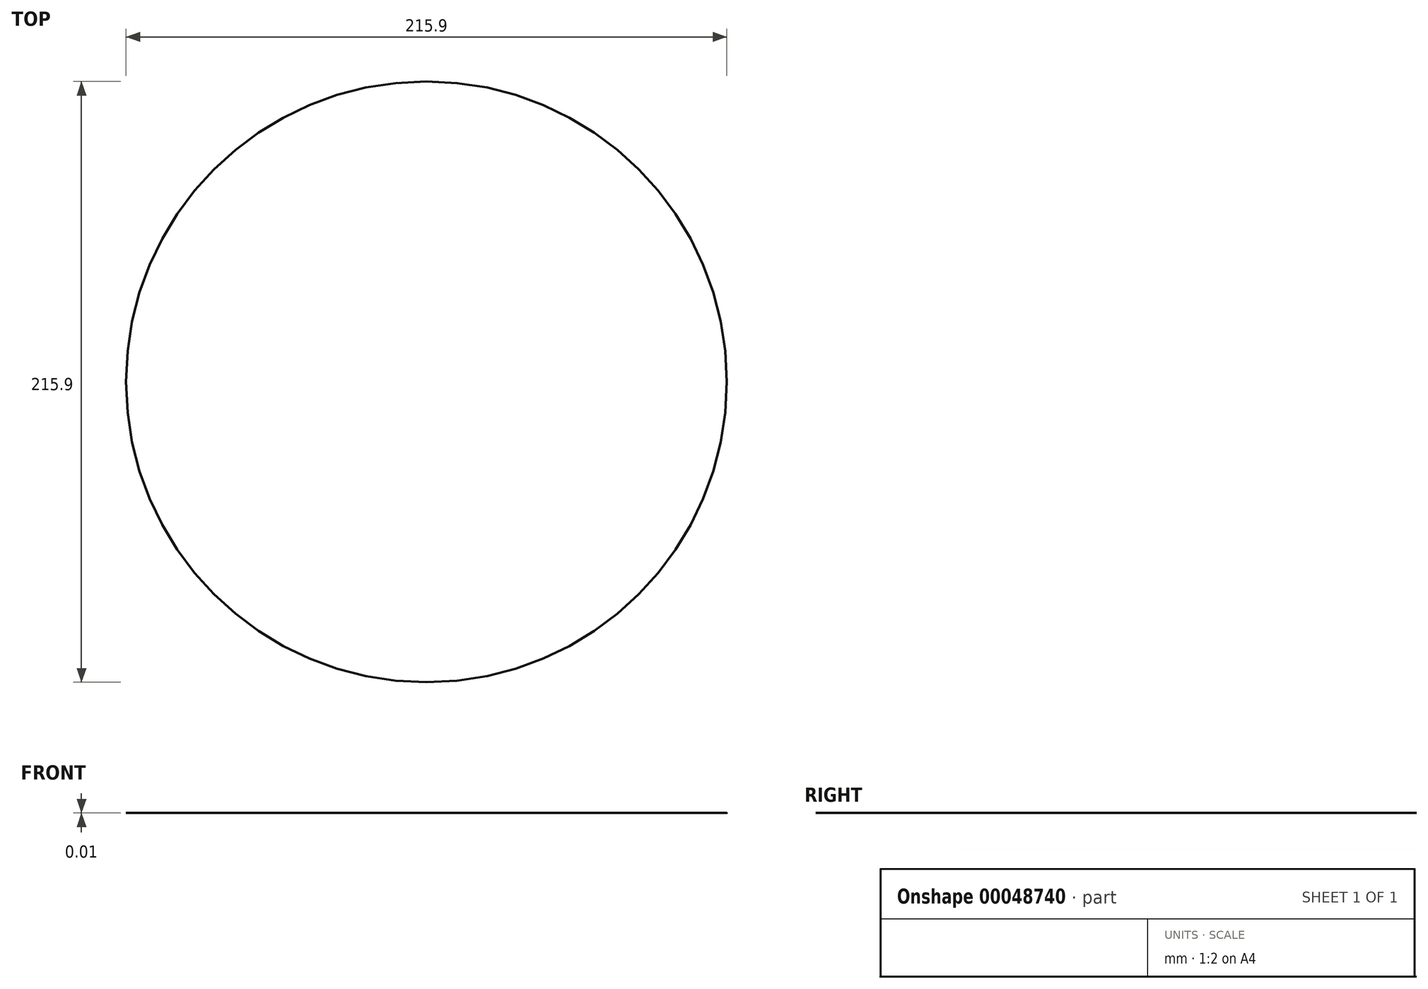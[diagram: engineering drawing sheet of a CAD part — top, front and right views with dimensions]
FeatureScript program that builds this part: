
annotation { "Feature Type Name" : "Feature", "Feature Type Description" : "" }
export const myFeature = defineFeature(function(context is Context, id is Id, definition is map)
    precondition{}
    {
        {
            var Q0;
            Q0=qCreatedBy(makeId("Top.planeOp"),FACE);
            var sketch = newSketch(context, id + "F0", { "sketchPlane" : qUnion([Q0])});
            skCircle(sketch, "E0", {"center": v(0, 0) * mm, "radius": 107.95 * mm});
            skSolve(sketch);
        }
        {
            var Q0;
            Q0=makeQuery(id+"F0.imprint","IMPRINT",FACE,{"disambiguationData":[TD([[makeQuery(id+"F0.imprint","IMPRINT",EDGE,{"derivedFrom":sQuery(id+"F0.wireOp",EDGE,"E0")}),1.0]])]});
            extrude(context, id + "F1", {"entities" : qUnion([Q0]), "depth" : 3 / 406.4 * mm});
        }
    });
